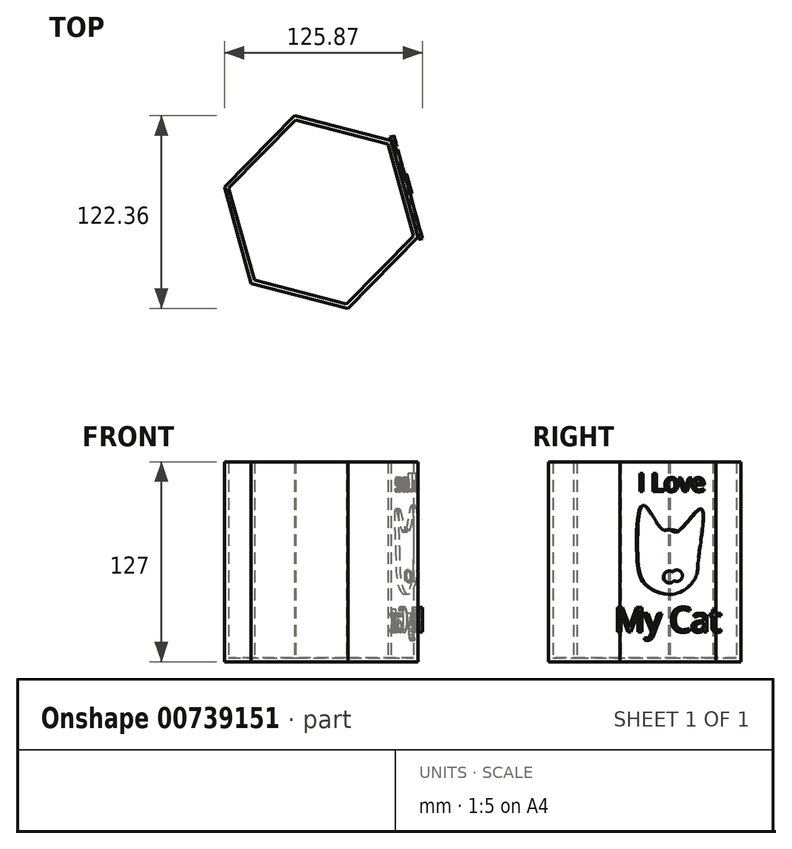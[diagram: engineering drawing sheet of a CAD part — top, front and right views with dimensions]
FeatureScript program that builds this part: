
annotation { "Feature Type Name" : "Feature", "Feature Type Description" : "" }
export const myFeature = defineFeature(function(context is Context, id is Id, definition is map)
    precondition{}
    {
        {
            var Q0;
            Q0=qCreatedBy(makeId("Top.planeOp"),FACE);
            var sketch = newSketch(context, id + "F0", { "sketchPlane" : qUnion([Q0])});
            skCircle(sketch, "E0.cCircle", {"center": v(0, 0) * mm, "radius": 55 * mm, "construction": true});
            skLineSegment(sketch, "E0.0", {"start": v(-44.48, -45.32) * mm, "end": v(-61.49, 15.87) * mm});
            skLineSegment(sketch, "E0.1", {"start": v(-61.49, 15.87) * mm, "end": v(-17, 61.18) * mm});
            skLineSegment(sketch, "E0.2", {"start": v(-17, 61.18) * mm, "end": v(44.48, 45.32) * mm});
            skLineSegment(sketch, "E0.3", {"start": v(44.48, 45.32) * mm, "end": v(61.49, -15.87) * mm});
            skLineSegment(sketch, "E0.4", {"start": v(61.49, -15.87) * mm, "end": v(17, -61.18) * mm});
            skLineSegment(sketch, "E0.5", {"start": v(17, -61.18) * mm, "end": v(-44.48, -45.32) * mm});
            skPoint(sketch, "E0.0.midPoint", {"position": v(-52.98, -14.73) * mm});
            skSolve(sketch);
        }
        {
            var Q0;
            Q0=makeQuery(id+"F0.imprint","IMPRINT",FACE,{"disambiguationData":[TD([[makeQuery(id+"F0.imprint","IMPRINT",EDGE,{"derivedFrom":sQuery(id+"F0.wireOp",EDGE,"E0.0")}),-1.0]])]});
            extrude(context, id + "F1", {"entities" : qUnion([Q0]), "depth" : 127 * mm, "offsetDistance" : 25.4 * mm});
        }
        {
            var Q0;
            Q0=makeQuery(id+"F1.opExtrude","CAP_FACE",FACE,{"disambiguationData":[OSD([sQuery(id+"F0.wireOp",EDGE,"E0.0"),sQuery(id+"F0.wireOp",EDGE,"E0.1"),sQuery(id+"F0.wireOp",EDGE,"E0.2"),sQuery(id+"F0.wireOp",EDGE,"E0.3"),sQuery(id+"F0.wireOp",EDGE,"E0.4"),sQuery(id+"F0.wireOp",EDGE,"E0.5")])],"isStart":false});
            shell(context, id + "F2", {"entities" : qUnion([Q0]), "thickness" : 2.54 * mm});
        }
        {
            var Q0;
            Q0=makeQuery(id+"F1.opExtrude","SWEPT_FACE",FACE,{"disambiguationData":[OSD([sQuery(id+"F0.wireOp",EDGE,"E0.3")])]});
            var sketch = newSketch(context, id + "F3", { "sketchPlane" : qUnion([Q0])});
            skCircle(sketch, "E1", {"center": v(0, 63.5) * mm, "radius": 20.43 * mm});
            skPoint(sketch, "E1.centerSnap0", {"position": v(-31.75, 63.5) * mm});
            skFitSpline(sketch, "E2", {"points": [v(18.2, 72.77) * mm, v(15.65, 99.29) * mm, v(6.03, 83.02) * mm, v(0, 83.93) * mm, v(-6.01, 83.03) * mm, v(-15.62, 102.1) * mm, v(-18.56, 72.04) * mm, v(-20.34, 65.42) * mm, v(-19.53, 57.5) * mm, v(-17.72, 53.33) * mm, v(-15.2, 49.85) * mm, v(-7.41, 44.46) * mm, v(0, 43.07) * mm, v(7.76, 44.6) * mm, v(13.31, 48) * mm, v(18.39, 54.6) * mm, v(20.38, 62.11) * mm, v(20.24, 66.26) * mm, v(18.2, 72.77) * mm]});
            skSolve(sketch);
        }
        {
            var Q0;
            {var subQ0=sQuery(id+"F3.wireOp",EDGE,"E2");var subQ1=sQuery(id+"F3.wireOp",EDGE,"E1");var subQ12=makeQuery(id+"F3.imprint","INTERSECT",VERTEX,{"disambiguationData":[OD(2.0)],"derivedFrom":[subQ1,subQ0]});Q0=makeQuery(id+"F3.imprint","IMPRINT",FACE,{"disambiguationData":[TD([[makeQuery(id+"F3.imprint","IMPRINT",EDGE,{"disambiguationData":[TD([[subQ12,-1.0]])],"derivedFrom":subQ1}),1.0]])]});}
            extrude(context, id + "F4", {"entities" : qUnion([Q0]), "depth" : 2.54 * mm, "offsetDistance" : 25.4 * mm});
        }
        {
            var Q0;
            Q0=makeQuery(id+"F1.opExtrude","SWEPT_FACE",FACE,{"disambiguationData":[OSD([sQuery(id+"F0.wireOp",EDGE,"E0.3")])]});
            var sketch = newSketch(context, id + "F5", { "sketchPlane" : qUnion([Q0])});
            skFitSpline(sketch, "E3", {"points": [v(19.56, 66.35) * mm, v(21.33, 96.98) * mm, v(5.59, 82.66) * mm, v(0, 83.88) * mm, v(-4.33, 84) * mm, v(-16.9, 99.42) * mm, v(-20.54, 66.3) * mm, v(-19.1, 56.02) * mm, v(-15.21, 49.18) * mm, v(0, 42.82) * mm, v(13.48, 48.18) * mm, v(18.53, 56.3) * mm, v(19.56, 66.35) * mm]});
            skSolve(sketch);
        }
        {
            var Q0;
            Q0 = qSketchRegion(id + "F5", true);
            extrude(context, id + "F6", {"entities" : qUnion([Q0]), "operationType" : NewBodyOperationType.ADD, "depth" : 2.54 * mm, "offsetDistance" : 25.4 * mm});
        }
        {
            var Q0;
            Q0=makeQuery(id+"F6.boolean.opBoolean","MERGE",FACE,{"derivedFrom":[makeQuery(id+"F4.opExtrude","CAP_FACE",FACE,{"disambiguationData":[OSD([sQuery(id+"F3.wireOp",EDGE,"E1"),sQuery(id+"F3.wireOp",EDGE,"E2")])],"isStart":false}),makeQuery(id+"F6.opExtrude","CAP_FACE",FACE,{"disambiguationData":[OSD([sQuery(id+"F5.wireOp",EDGE,"E3")])],"isStart":false})]});
            var sketch = newSketch(context, id + "F7", { "sketchPlane" : qUnion([Q0])});
            skCircle(sketch, "E4", {"center": v(-8.23, 66.24) * mm, "radius": 3.4 * mm});
            skCircle(sketch, "E5", {"center": v(9.37, 67.12) * mm, "radius": 3.4 * mm});
            skSolve(sketch);
        }
        {
            var Q0;
            Q0=sQuery(id+"F7.wireOp",VERTEX,"E4.center");
            var Q1;
            Q1=makeQuery(id+"F4.opExtrude","SWEPT_BODY",BODY,{"disambiguationData":[OSD([sQuery(id+"F3.wireOp",EDGE,"E1"),sQuery(id+"F3.wireOp",EDGE,"E2")])]});
            hole(context, id + "F8", {"style" : HoleStyle.SIMPLE, "endStyle" : HoleEndStyle.BLIND, "holeDiameter" : 6.78 * mm, "majorDiameter" : 6.35 * mm, "holeDepth" : 2.54 * mm, "isTappedThrough" : true, "tappedDepth" : 12.7 * mm, "tapClearance" : 3, "startFromSketch" : true, "locations" : qUnion([Q0]), "scope" : qUnion([Q1])});
        }
        {
            var Q0;
            Q0=makeQuery(id+"F6.boolean.opBoolean","MERGE",FACE,{"derivedFrom":[makeQuery(id+"F4.opExtrude","CAP_FACE",FACE,{"disambiguationData":[OSD([sQuery(id+"F3.wireOp",EDGE,"E1"),sQuery(id+"F3.wireOp",EDGE,"E2")])],"isStart":false}),makeQuery(id+"F6.opExtrude","CAP_FACE",FACE,{"disambiguationData":[OSD([sQuery(id+"F5.wireOp",EDGE,"E3")])],"isStart":false})]});
            var sketch = newSketch(context, id + "F9", { "sketchPlane" : qUnion([Q0])});
            skCircle(sketch, "E6", {"center": v(10.95, 65.54) * mm, "radius": 1.95 * mm});
            skSolve(sketch);
        }
        {
            var Q0;
            Q0=sQuery(id+"F9.wireOp",VERTEX,"E6.center");
            var Q1;
            Q1=makeQuery(id+"F4.opExtrude","SWEPT_BODY",BODY,{"disambiguationData":[OSD([sQuery(id+"F3.wireOp",EDGE,"E1"),sQuery(id+"F3.wireOp",EDGE,"E2")])]});
            hole(context, id + "F10", {"style" : HoleStyle.SIMPLE, "endStyle" : HoleEndStyle.BLIND, "holeDiameter" : 6.78 * mm, "majorDiameter" : 6.35 * mm, "holeDepth" : 2.54 * mm, "isTappedThrough" : true, "tappedDepth" : 12.7 * mm, "tapClearance" : 3, "startFromSketch" : true, "locations" : qUnion([Q0]), "scope" : qUnion([Q1])});
        }
        {
            var Q0;
            Q0=makeQuery(id+"F6.boolean.opBoolean","MERGE",FACE,{"derivedFrom":[makeQuery(id+"F4.opExtrude","CAP_FACE",FACE,{"disambiguationData":[OSD([sQuery(id+"F3.wireOp",EDGE,"E1"),sQuery(id+"F3.wireOp",EDGE,"E2")])],"isStart":false}),makeQuery(id+"F6.opExtrude","CAP_FACE",FACE,{"disambiguationData":[OSD([sQuery(id+"F5.wireOp",EDGE,"E3")])],"isStart":false})]});
            var sketch = newSketch(context, id + "F11", { "sketchPlane" : qUnion([Q0])});
            skCircle(sketch, "E7", {"center": v(4.9, 54.7) * mm, "radius": 3.6 * mm});
            skCircle(sketch, "E8", {"center": v(0, 53.85) * mm, "radius": 3.81 * mm});
            skSolve(sketch);
        }
        {
            var Q0;
            {var subQ0=sQuery(id+"F11.wireOp",EDGE,"E8");var subQ1=sQuery(id+"F11.wireOp",EDGE,"E7");var subQ2=makeQuery(id+"F11.imprint","INTERSECT",VERTEX,{"disambiguationData":[OD(0.0)],"derivedFrom":[subQ1,subQ0]});Q0=makeQuery(id+"F11.imprint","IMPRINT",FACE,{"disambiguationData":[TD([[makeQuery(id+"F11.imprint","IMPRINT",EDGE,{"disambiguationData":[TD([[subQ2,1.0]])],"derivedFrom":subQ1}),-1.0]])]});}
            var Q1;
            {var subQ0=sQuery(id+"F11.wireOp",EDGE,"E8");var subQ1=sQuery(id+"F11.wireOp",EDGE,"E7");var subQ2=makeQuery(id+"F11.imprint","INTERSECT",VERTEX,{"disambiguationData":[OD(0.0)],"derivedFrom":[subQ1,subQ0]});Q1=makeQuery(id+"F11.imprint","IMPRINT",FACE,{"disambiguationData":[TD([[makeQuery(id+"F11.imprint","IMPRINT",EDGE,{"disambiguationData":[TD([[subQ2,1.0]])],"derivedFrom":subQ1}),1.0]])]});}
            var Q2;
            {var subQ0=sQuery(id+"F11.wireOp",EDGE,"E8");var subQ1=sQuery(id+"F11.wireOp",EDGE,"E7");var subQ2=makeQuery(id+"F11.imprint","INTERSECT",VERTEX,{"disambiguationData":[OD(0.0)],"derivedFrom":[subQ1,subQ0]});Q2=makeQuery(id+"F11.imprint","IMPRINT",FACE,{"disambiguationData":[TD([[makeQuery(id+"F11.imprint","IMPRINT",EDGE,{"disambiguationData":[TD([[subQ2,-1.0]])],"derivedFrom":subQ1}),1.0]])]});}
            extrude(context, id + "F12", {"entities" : qUnion([Q0, Q1, Q2]), "operationType" : NewBodyOperationType.ADD, "depth" : 1.27 * mm, "offsetDistance" : 25.4 * mm});
        }
        {
            var Q0;
            Q0=makeQuery(id+"F6.boolean.opBoolean","MERGE",FACE,{"derivedFrom":[makeQuery(id+"F4.opExtrude","CAP_FACE",FACE,{"disambiguationData":[OSD([sQuery(id+"F3.wireOp",EDGE,"E1"),sQuery(id+"F3.wireOp",EDGE,"E2")])],"isStart":false}),makeQuery(id+"F6.opExtrude","CAP_FACE",FACE,{"disambiguationData":[OSD([sQuery(id+"F5.wireOp",EDGE,"E3")])],"isStart":false})]});
            var sketch = newSketch(context, id + "F13", { "sketchPlane" : qUnion([Q0])});
            skCircle(sketch, "E9", {"center": v(3.08, 51.6) * mm, "radius": 2.25 * mm});
            skSolve(sketch);
        }
        {
            var Q0;
            Q0=sQuery(id+"F13.wireOp",VERTEX,"E9.center");
            var Q1;
            Q1=makeQuery(id+"F4.opExtrude","SWEPT_BODY",BODY,{"disambiguationData":[OSD([sQuery(id+"F3.wireOp",EDGE,"E1"),sQuery(id+"F3.wireOp",EDGE,"E2")])]});
            hole(context, id + "F14", {"style" : HoleStyle.SIMPLE, "endStyle" : HoleEndStyle.BLIND, "holeDiameter" : 6.78 * mm, "majorDiameter" : 6.35 * mm, "holeDepth" : 2.54 * mm, "isTappedThrough" : true, "tappedDepth" : 12.7 * mm, "tapClearance" : 3, "startFromSketch" : true, "locations" : qUnion([Q0]), "scope" : qUnion([Q1])});
        }
        {
            var Q0;
            Q0=makeQuery(id+"F1.opExtrude","SWEPT_FACE",FACE,{"disambiguationData":[OSD([sQuery(id+"F0.wireOp",EDGE,"E0.3")])]});
            var sketch = newSketch(context, id + "F15", { "sketchPlane" : qUnion([Q0])});
            skText(sketch, "E10", { "text": "I Love", "fontName": "OpenSans-Regular.ttf"});
            skText(sketch, "E11", { "text": "My Cat", "fontName": "OpenSans-Regular.ttf"});
            const initialGuessF15  = {"E10": [-0.02007, 0.10817, 1, 0, 0.01167], "E11": [-0.03556, 0.01895, 1, 0, 0.01576]};
            skSetInitialGuess(sketch, initialGuessF15);
            skSolve(sketch);
        }
        {
            var Q0;
            Q0 = qSketchRegion(id + "F15", true);
            extrude(context, id + "F16", {"entities" : qUnion([Q0]), "depth" : 2.54 * mm, "offsetDistance" : 25.4 * mm});
        }
    });
